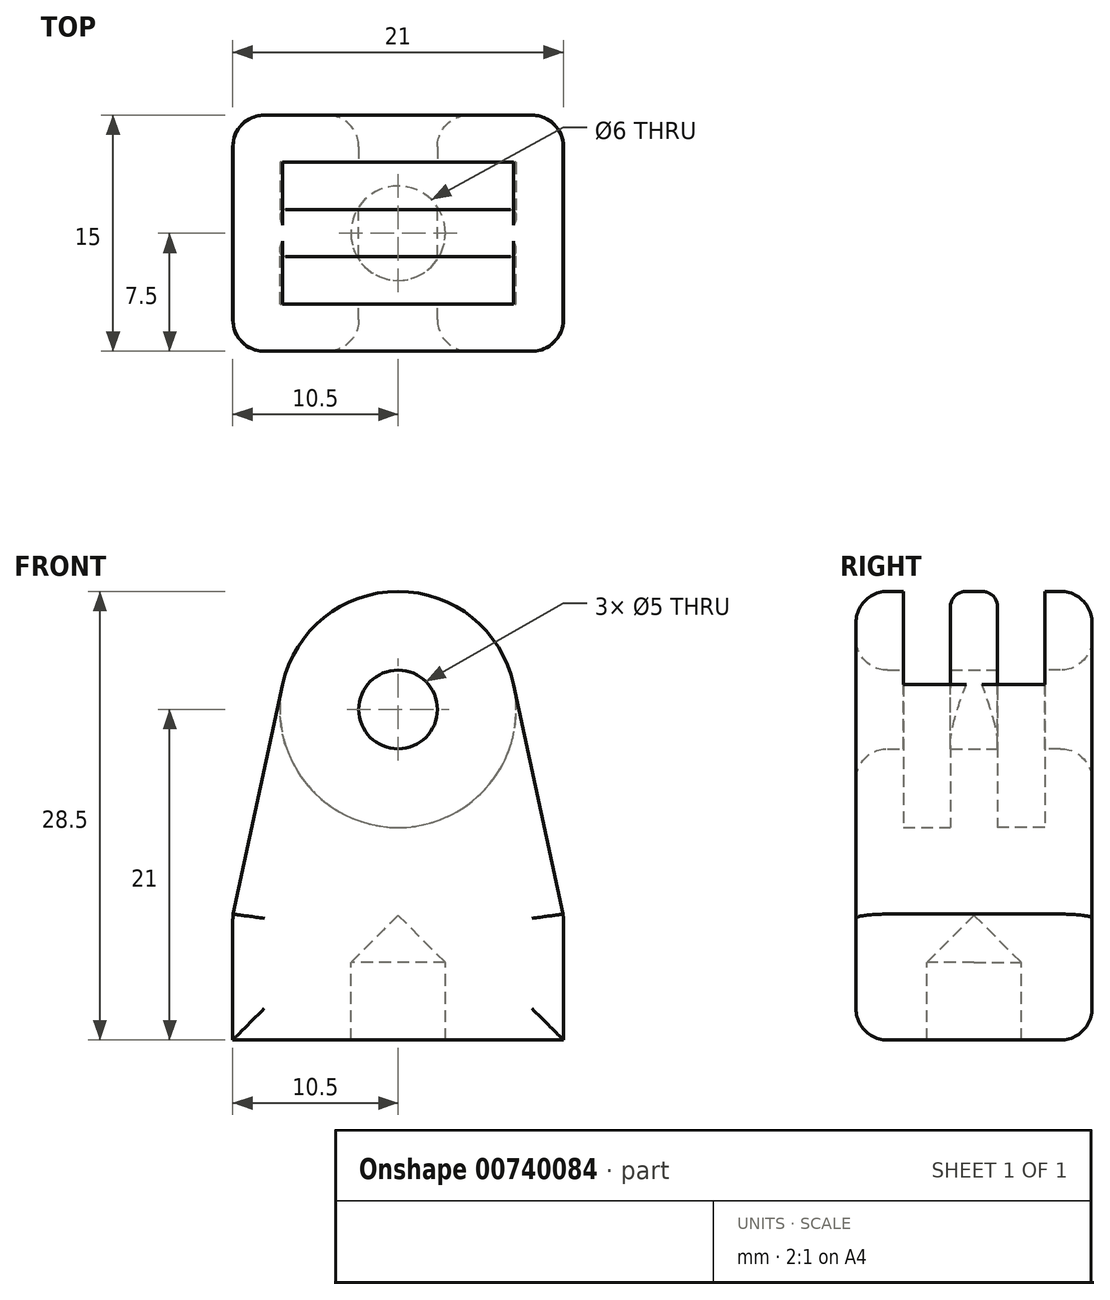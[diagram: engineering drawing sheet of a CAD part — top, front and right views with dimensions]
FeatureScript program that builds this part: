
annotation { "Feature Type Name" : "Feature", "Feature Type Description" : "" }
export const myFeature = defineFeature(function(context is Context, id is Id, definition is map)
    precondition{}
    {
        {
            var Q0;
            Q0=qCreatedBy(makeId("Front.planeOp"),FACE);
            var sketch = newSketch(context, id + "F0", { "sketchPlane" : qUnion([Q0])});
            skCircle(sketch, "E0", {"center": v(0, 0) * mm, "radius": 2.5 * mm});
            skCircle(sketch, "E1", {"center": v(0, 0) * mm, "radius": 7.5 * mm});
            skLineSegment(sketch, "E2", {"start": v(-7.33, 1.58) * mm, "end": v(-10.5, -13.08) * mm});
            skLineSegment(sketch, "E3", {"start": v(7.33, 1.58) * mm, "end": v(10.5, -13.08) * mm});
            skLineSegment(sketch, "E4", {"start": v(-10.5, -13.08) * mm, "end": v(10.5, -13.08) * mm});
            skSolve(sketch);
        }
        {
            var Q0;
            Q0=makeQuery(id+"F0.imprint","IMPRINT",FACE,{"disambiguationData":[TD([[makeQuery(id+"F0.imprint","IMPRINT",EDGE,{"derivedFrom":sQuery(id+"F0.wireOp",EDGE,"E0")}),-1.0]])]});
            extrude(context, id + "F1", {"entities" : qUnion([Q0]), "depth" : (7.5) * mm, "offsetDistance" : 25 * mm});
        }
        {
            var Q0;
            Q0=qCreatedBy(makeId("Front.planeOp"),FACE);
            cPlane(context, id + "F2", {"entities" : qUnion([Q0]), "cplaneType" : CPlaneType.OFFSET, "offset" : 1.5 * mm, "width" : 150 * mm, "height" : 150 * mm});
        }
        {
            var Q0;
            Q0=qCreatedBy(id+"F2.planeOp",FACE);
            var sketch = newSketch(context, id + "F3", { "sketchPlane" : qUnion([Q0])});
            skCircle(sketch, "E5", {"center": v(0, 0) * mm, "radius": 2.5 * mm});
            skCircle(sketch, "E6", {"center": v(0, 0) * mm, "radius": 7.5 * mm});
            skLineSegment(sketch, "E7", {"start": v(-7.33, 1.58) * mm, "end": v(-10.5, -13.08) * mm});
            skLineSegment(sketch, "E8", {"start": v(7.33, 1.58) * mm, "end": v(10.5, -13.08) * mm});
            skLineSegment(sketch, "E9", {"start": v(-10.5, -13.08) * mm, "end": v(10.5, -13.08) * mm});
            skSolve(sketch);
        }
        {
            var Q0;
            Q0=makeQuery(id+"F3.imprint","IMPRINT",FACE,{"disambiguationData":[TD([[makeQuery(id+"F3.imprint","IMPRINT",EDGE,{"derivedFrom":sQuery(id+"F3.wireOp",EDGE,"E5")}),-1.0]])]});
            extrude(context, id + "F4", {"entities" : qUnion([Q0]), "operationType" : NewBodyOperationType.REMOVE, "depth" : 3 * mm, "offsetDistance" : 25 * mm});
        }
        {
            var Q0;
            {var subQ0=sQuery(id+"F0.wireOp",EDGE,"E2");Q0=makeQuery(id+"F0.imprint","IMPRINT",FACE,{"disambiguationData":[TD([[makeQuery(id+"F0.imprint","IMPRINT",EDGE,{"derivedFrom":subQ0}),1.0]])]});}
            extrude(context, id + "F5", {"entities" : qUnion([Q0]), "operationType" : NewBodyOperationType.ADD, "depth" : 7.5 * mm, "offsetDistance" : 25 * mm});
        }
        {
            var Q0;
            Q0=makeQuery(id+"F4.boolean.opBoolean","SPLIT",BODY,{"disambiguationData":[OD(0.0)],"derivedFrom":makeQuery(id+"F1.opExtrude","SWEPT_BODY",BODY,{"disambiguationData":[OSD([sQuery(id+"F0.wireOp",EDGE,"E0"),sQuery(id+"F0.wireOp",EDGE,"E1")])]})});
            var Q1;
            Q1=qCreatedBy(makeId("Front.planeOp"),FACE);
            mirror(context, id + "F6", {"operationType" : NewBodyOperationType.ADD, "entities" : qUnion([Q0]), "mirrorPlane" : qUnion([Q1])});
        }
        {
            var Q0;
            Q0=qCreatedBy(makeId("Top.planeOp"),FACE);
            cPlane(context, id + "F7", {"entities" : qUnion([Q0]), "cplaneType" : CPlaneType.OFFSET, "offset" : 13 * mm, "oppositeDirection" : true, "width" : 150 * mm, "height" : 150 * mm});
        }
        {
            var Q0;
            Q0=qCreatedBy(id+"F7.planeOp",FACE);
            var sketch = newSketch(context, id + "F8", { "sketchPlane" : qUnion([Q0])});
            skCircle(sketch, "E10", {"center": v(0, 0) * mm, "radius": 3 * mm});
            skLineSegment(sketch, "E11.bottom", {"start": v(10.5, 7.5) * mm, "end": v(-10.5, 7.5) * mm});
            skLineSegment(sketch, "E11.top", {"start": v(10.5, -7.5) * mm, "end": v(-10.5, -7.5) * mm});
            skLineSegment(sketch, "E11.left", {"start": v(10.5, 7.5) * mm, "end": v(10.5, -7.5) * mm});
            skLineSegment(sketch, "E11.right", {"start": v(-10.5, 7.5) * mm, "end": v(-10.5, -7.5) * mm});
            skSolve(sketch);
        }
        {
            var Q0;
            Q0=makeQuery(id+"F8.imprint","IMPRINT",FACE,{"disambiguationData":[TD([[makeQuery(id+"F8.imprint","IMPRINT",EDGE,{"derivedFrom":sQuery(id+"F8.wireOp",EDGE,"E10")}),-1.0]])]});
            extrude(context, id + "F9", {"entities" : qUnion([Q0]), "operationType" : NewBodyOperationType.ADD, "oppositeDirection" : true, "depth" : 8 * mm, "offsetDistance" : 25 * mm});
        }
        {
            var Q0;
            {var subQ0=makeQuery(id+"F5.opExtrude","SWEPT_FACE",FACE,{"disambiguationData":[OSD([sQuery(id+"F0.wireOp",EDGE,"E4")])]});Q0=makeQuery(id+"F9.boolean.opBoolean","INTERSECT",EDGE,{"derivedFrom":[makeQuery(id+"F6.boolean.opBoolean","MERGE",FACE,{"derivedFrom":[subQ0,makeQuery(id+"F6.opPattern","COPY",FACE,{"derivedFrom":subQ0,"instanceName":"1"})]}),makeQuery(id+"F9.opExtrude","SWEPT_FACE",FACE,{"disambiguationData":[OSD([sQuery(id+"F8.wireOp",EDGE,"E10")])]})]});}
            chamfer(context, id + "F10", {"entities" : qUnion([Q0]), "width" : 3 * mm, "tangentPropagation" : true});
        }
        {
            var Q0;
            Q0=makeQuery(id+"F9.opExtrude","CAP_EDGE",EDGE,{"disambiguationData":[OSD([sQuery(id+"F8.wireOp",EDGE,"E11.left")])],"isStart":true});
            var Q1;
            Q1=makeQuery(id+"F9.opExtrude","CAP_EDGE",EDGE,{"disambiguationData":[OSD([sQuery(id+"F8.wireOp",EDGE,"E11.right")])],"isStart":true});
            fillet(context, id + "F11", {"entities" : qUnion([Q0, Q1]), "radius" : 10 * mm, "tangentPropagation" : true, "allowEdgeOverflow" : false});
        }
        {
            var Q0;
            Q0=makeQuery(id+"F5.opExtrude","CAP_EDGE",EDGE,{"disambiguationData":[OSD([sQuery(id+"F0.wireOp",EDGE,"E2")])],"isStart":false});
            var Q1;
            Q1=makeQuery(id+"F9.opExtrude","SWEPT_EDGE",EDGE,{"disambiguationData":[OSD([sQuery(id+"F8.wireOp",EDGE,"E11.top"),sQuery(id+"F8.wireOp",EDGE,"E11.right")])]});
            var Q2;
            Q2=makeQuery(id+"F9.opExtrude","SWEPT_EDGE",EDGE,{"disambiguationData":[OSD([sQuery(id+"F8.wireOp",EDGE,"E11.top"),sQuery(id+"F8.wireOp",EDGE,"E11.left")])]});
            var Q3;
            {var subQ0=sQuery(id+"F0.wireOp",EDGE,"E1");Q3=makeQuery(id+"F11.opFillet","BLEND_EDGE",EDGE,{"blendedFrom":[makeQuery(id+"F9.opExtrude","CAP_EDGE",EDGE,{"disambiguationData":[OSD([sQuery(id+"F8.wireOp",EDGE,"E11.left")])],"isStart":true}),makeQuery(id+"F9.boolean.opBoolean","MERGE",FACE,{"derivedFrom":[makeQuery(id+"F5.boolean.opBoolean","MERGE",FACE,{"derivedFrom":[makeQuery(id+"F1.opExtrude","CAP_FACE",FACE,{"disambiguationData":[OSD([sQuery(id+"F0.wireOp",EDGE,"E0"),subQ0])],"isStart":false}),makeQuery(id+"F5.opExtrude","CAP_FACE",FACE,{"disambiguationData":[OSD([subQ0,sQuery(id+"F0.wireOp",EDGE,"E2"),sQuery(id+"F0.wireOp",EDGE,"E3"),sQuery(id+"F0.wireOp",EDGE,"E4")])],"isStart":false})]}),makeQuery(id+"F9.opExtrude","SWEPT_FACE",FACE,{"disambiguationData":[OSD([sQuery(id+"F8.wireOp",EDGE,"E11.top")])]})]})],"blendedInto":[makeQuery(id+"F9.boolean.opBoolean","MERGE",FACE,{"derivedFrom":[makeQuery(id+"F5.boolean.opBoolean","MERGE",FACE,{"derivedFrom":[makeQuery(id+"F1.opExtrude","CAP_FACE",FACE,{"disambiguationData":[OSD([sQuery(id+"F0.wireOp",EDGE,"E0"),subQ0])],"isStart":false}),makeQuery(id+"F5.opExtrude","CAP_FACE",FACE,{"disambiguationData":[OSD([subQ0,sQuery(id+"F0.wireOp",EDGE,"E2"),sQuery(id+"F0.wireOp",EDGE,"E3"),sQuery(id+"F0.wireOp",EDGE,"E4")])],"isStart":false})]}),makeQuery(id+"F9.opExtrude","SWEPT_FACE",FACE,{"disambiguationData":[OSD([sQuery(id+"F8.wireOp",EDGE,"E11.top")])]})]})]});}
            var Q4;
            {var subQ0=sQuery(id+"F0.wireOp",EDGE,"E1");Q4=makeQuery(id+"F11.opFillet","BLEND_EDGE",EDGE,{"blendedFrom":[makeQuery(id+"F9.opExtrude","CAP_EDGE",EDGE,{"disambiguationData":[OSD([sQuery(id+"F8.wireOp",EDGE,"E11.right")])],"isStart":true}),makeQuery(id+"F9.boolean.opBoolean","MERGE",FACE,{"derivedFrom":[makeQuery(id+"F5.boolean.opBoolean","MERGE",FACE,{"derivedFrom":[makeQuery(id+"F1.opExtrude","CAP_FACE",FACE,{"disambiguationData":[OSD([sQuery(id+"F0.wireOp",EDGE,"E0"),subQ0])],"isStart":false}),makeQuery(id+"F5.opExtrude","CAP_FACE",FACE,{"disambiguationData":[OSD([subQ0,sQuery(id+"F0.wireOp",EDGE,"E2"),sQuery(id+"F0.wireOp",EDGE,"E3"),sQuery(id+"F0.wireOp",EDGE,"E4")])],"isStart":false})]}),makeQuery(id+"F9.opExtrude","SWEPT_FACE",FACE,{"disambiguationData":[OSD([sQuery(id+"F8.wireOp",EDGE,"E11.top")])]})]})],"blendedInto":[makeQuery(id+"F9.boolean.opBoolean","MERGE",FACE,{"derivedFrom":[makeQuery(id+"F5.boolean.opBoolean","MERGE",FACE,{"derivedFrom":[makeQuery(id+"F1.opExtrude","CAP_FACE",FACE,{"disambiguationData":[OSD([sQuery(id+"F0.wireOp",EDGE,"E0"),subQ0])],"isStart":false}),makeQuery(id+"F5.opExtrude","CAP_FACE",FACE,{"disambiguationData":[OSD([subQ0,sQuery(id+"F0.wireOp",EDGE,"E2"),sQuery(id+"F0.wireOp",EDGE,"E3"),sQuery(id+"F0.wireOp",EDGE,"E4")])],"isStart":false})]}),makeQuery(id+"F9.opExtrude","SWEPT_FACE",FACE,{"disambiguationData":[OSD([sQuery(id+"F8.wireOp",EDGE,"E11.top")])]})]})]});}
            var Q5;
            Q5=makeQuery(id+"F6.opPattern","COPY",EDGE,{"derivedFrom":makeQuery(id+"F5.opExtrude","CAP_EDGE",EDGE,{"disambiguationData":[OSD([sQuery(id+"F0.wireOp",EDGE,"E3")])],"isStart":false}),"instanceName":"1"});
            var Q6;
            Q6=makeQuery(id+"F9.opExtrude","SWEPT_EDGE",EDGE,{"disambiguationData":[OSD([sQuery(id+"F8.wireOp",EDGE,"E11.bottom"),sQuery(id+"F8.wireOp",EDGE,"E11.left")])]});
            var Q7;
            {var subQ0=sQuery(id+"F0.wireOp",EDGE,"E1");Q7=makeQuery(id+"F11.opFillet","BLEND_EDGE",EDGE,{"blendedFrom":[makeQuery(id+"F9.opExtrude","CAP_EDGE",EDGE,{"disambiguationData":[OSD([sQuery(id+"F8.wireOp",EDGE,"E11.left")])],"isStart":true}),makeQuery(id+"F9.boolean.opBoolean","MERGE",FACE,{"derivedFrom":[makeQuery(id+"F6.opPattern","COPY",FACE,{"derivedFrom":makeQuery(id+"F5.boolean.opBoolean","MERGE",FACE,{"derivedFrom":[makeQuery(id+"F1.opExtrude","CAP_FACE",FACE,{"disambiguationData":[OSD([sQuery(id+"F0.wireOp",EDGE,"E0"),subQ0])],"isStart":false}),makeQuery(id+"F5.opExtrude","CAP_FACE",FACE,{"disambiguationData":[OSD([subQ0,sQuery(id+"F0.wireOp",EDGE,"E2"),sQuery(id+"F0.wireOp",EDGE,"E3"),sQuery(id+"F0.wireOp",EDGE,"E4")])],"isStart":false})]}),"instanceName":"1"}),makeQuery(id+"F9.opExtrude","SWEPT_FACE",FACE,{"disambiguationData":[OSD([sQuery(id+"F8.wireOp",EDGE,"E11.bottom")])]})]})],"blendedInto":[makeQuery(id+"F9.boolean.opBoolean","MERGE",FACE,{"derivedFrom":[makeQuery(id+"F6.opPattern","COPY",FACE,{"derivedFrom":makeQuery(id+"F5.boolean.opBoolean","MERGE",FACE,{"derivedFrom":[makeQuery(id+"F1.opExtrude","CAP_FACE",FACE,{"disambiguationData":[OSD([sQuery(id+"F0.wireOp",EDGE,"E0"),subQ0])],"isStart":false}),makeQuery(id+"F5.opExtrude","CAP_FACE",FACE,{"disambiguationData":[OSD([subQ0,sQuery(id+"F0.wireOp",EDGE,"E2"),sQuery(id+"F0.wireOp",EDGE,"E3"),sQuery(id+"F0.wireOp",EDGE,"E4")])],"isStart":false})]}),"instanceName":"1"}),makeQuery(id+"F9.opExtrude","SWEPT_FACE",FACE,{"disambiguationData":[OSD([sQuery(id+"F8.wireOp",EDGE,"E11.bottom")])]})]})]});}
            var Q8;
            Q8=makeQuery(id+"F9.opExtrude","SWEPT_EDGE",EDGE,{"disambiguationData":[OSD([sQuery(id+"F8.wireOp",EDGE,"E11.bottom"),sQuery(id+"F8.wireOp",EDGE,"E11.right")])]});
            var Q9;
            {var subQ0=sQuery(id+"F0.wireOp",EDGE,"E1");Q9=makeQuery(id+"F11.opFillet","BLEND_EDGE",EDGE,{"blendedFrom":[makeQuery(id+"F9.opExtrude","CAP_EDGE",EDGE,{"disambiguationData":[OSD([sQuery(id+"F8.wireOp",EDGE,"E11.right")])],"isStart":true}),makeQuery(id+"F9.boolean.opBoolean","MERGE",FACE,{"derivedFrom":[makeQuery(id+"F6.opPattern","COPY",FACE,{"derivedFrom":makeQuery(id+"F5.boolean.opBoolean","MERGE",FACE,{"derivedFrom":[makeQuery(id+"F1.opExtrude","CAP_FACE",FACE,{"disambiguationData":[OSD([sQuery(id+"F0.wireOp",EDGE,"E0"),subQ0])],"isStart":false}),makeQuery(id+"F5.opExtrude","CAP_FACE",FACE,{"disambiguationData":[OSD([subQ0,sQuery(id+"F0.wireOp",EDGE,"E2"),sQuery(id+"F0.wireOp",EDGE,"E3"),sQuery(id+"F0.wireOp",EDGE,"E4")])],"isStart":false})]}),"instanceName":"1"}),makeQuery(id+"F9.opExtrude","SWEPT_FACE",FACE,{"disambiguationData":[OSD([sQuery(id+"F8.wireOp",EDGE,"E11.bottom")])]})]})],"blendedInto":[makeQuery(id+"F9.boolean.opBoolean","MERGE",FACE,{"derivedFrom":[makeQuery(id+"F6.opPattern","COPY",FACE,{"derivedFrom":makeQuery(id+"F5.boolean.opBoolean","MERGE",FACE,{"derivedFrom":[makeQuery(id+"F1.opExtrude","CAP_FACE",FACE,{"disambiguationData":[OSD([sQuery(id+"F0.wireOp",EDGE,"E0"),subQ0])],"isStart":false}),makeQuery(id+"F5.opExtrude","CAP_FACE",FACE,{"disambiguationData":[OSD([subQ0,sQuery(id+"F0.wireOp",EDGE,"E2"),sQuery(id+"F0.wireOp",EDGE,"E3"),sQuery(id+"F0.wireOp",EDGE,"E4")])],"isStart":false})]}),"instanceName":"1"}),makeQuery(id+"F9.opExtrude","SWEPT_FACE",FACE,{"disambiguationData":[OSD([sQuery(id+"F8.wireOp",EDGE,"E11.bottom")])]})]})]});}
            var Q10;
            {var subQ0=sQuery(id+"F0.wireOp",EDGE,"E1");Q10=makeQuery(id+"F9.boolean.opBoolean","MERGE",FACE,{"derivedFrom":[makeQuery(id+"F6.opPattern","COPY",FACE,{"derivedFrom":makeQuery(id+"F5.boolean.opBoolean","MERGE",FACE,{"derivedFrom":[makeQuery(id+"F1.opExtrude","CAP_FACE",FACE,{"disambiguationData":[OSD([sQuery(id+"F0.wireOp",EDGE,"E0"),subQ0])],"isStart":false}),makeQuery(id+"F5.opExtrude","CAP_FACE",FACE,{"disambiguationData":[OSD([subQ0,sQuery(id+"F0.wireOp",EDGE,"E2"),sQuery(id+"F0.wireOp",EDGE,"E3"),sQuery(id+"F0.wireOp",EDGE,"E4")])],"isStart":false})]}),"instanceName":"1"}),makeQuery(id+"F9.opExtrude","SWEPT_FACE",FACE,{"disambiguationData":[OSD([sQuery(id+"F8.wireOp",EDGE,"E11.bottom")])]})]});}
            var Q11;
            {var subQ0=sQuery(id+"F0.wireOp",EDGE,"E1");Q11=makeQuery(id+"F9.boolean.opBoolean","MERGE",FACE,{"derivedFrom":[makeQuery(id+"F5.boolean.opBoolean","MERGE",FACE,{"derivedFrom":[makeQuery(id+"F1.opExtrude","CAP_FACE",FACE,{"disambiguationData":[OSD([sQuery(id+"F0.wireOp",EDGE,"E0"),subQ0])],"isStart":false}),makeQuery(id+"F5.opExtrude","CAP_FACE",FACE,{"disambiguationData":[OSD([subQ0,sQuery(id+"F0.wireOp",EDGE,"E2"),sQuery(id+"F0.wireOp",EDGE,"E3"),sQuery(id+"F0.wireOp",EDGE,"E4")])],"isStart":false})]}),makeQuery(id+"F9.opExtrude","SWEPT_FACE",FACE,{"disambiguationData":[OSD([sQuery(id+"F8.wireOp",EDGE,"E11.top")])]})]});}
            fillet(context, id + "F12", {"entities" : qUnion([Q0, Q1, Q2, Q3, Q4, Q5, Q6, Q7, Q8, Q9, Q10, Q11]), "radius" : 2 * mm, "tangentPropagation" : true, "allowEdgeOverflow" : false});
        }
        {
            var Q0;
            {var subQ0=sQuery(id+"F3.wireOp",EDGE,"E6");Q0=makeQuery(id+"F5.boolean.opBoolean","SPLIT",EDGE,{"disambiguationData":[topologyDisambiguationEdgeConnected([makeQuery(id+"F1.opExtrude","SWEPT_FACE",FACE,{"disambiguationData":[OSD([sQuery(id+"F0.wireOp",EDGE,"E1")])]})])],"derivedFrom":makeQuery(id+"F4.boolean.opBoolean","COPY",EDGE,{"derivedFrom":makeQuery(id+"F4.opExtrude","CAP_EDGE",EDGE,{"disambiguationData":[OSD([subQ0])],"isStart":false})})});}
            var Q1;
            {var subQ0=sQuery(id+"F3.wireOp",EDGE,"E6");Q1=makeQuery(id+"F6.opPattern","COPY",EDGE,{"derivedFrom":makeQuery(id+"F5.boolean.opBoolean","SPLIT",EDGE,{"disambiguationData":[topologyDisambiguationEdgeConnected([makeQuery(id+"F1.opExtrude","SWEPT_FACE",FACE,{"disambiguationData":[OSD([sQuery(id+"F0.wireOp",EDGE,"E1")])]})])],"derivedFrom":makeQuery(id+"F4.boolean.opBoolean","COPY",EDGE,{"derivedFrom":makeQuery(id+"F4.opExtrude","CAP_EDGE",EDGE,{"disambiguationData":[OSD([subQ0])],"isStart":true})})}),"instanceName":"1"});}
            var Q2;
            {var subQ0=sQuery(id+"F3.wireOp",EDGE,"E6");Q2=makeQuery(id+"F5.boolean.opBoolean","SPLIT",EDGE,{"disambiguationData":[topologyDisambiguationEdgeConnected([makeQuery(id+"F1.opExtrude","SWEPT_FACE",FACE,{"disambiguationData":[OSD([sQuery(id+"F0.wireOp",EDGE,"E1")])]})])],"derivedFrom":makeQuery(id+"F4.boolean.opBoolean","COPY",EDGE,{"derivedFrom":makeQuery(id+"F4.opExtrude","CAP_EDGE",EDGE,{"disambiguationData":[OSD([subQ0])],"isStart":true})})});}
            var Q3;
            {var subQ0=sQuery(id+"F3.wireOp",EDGE,"E6");Q3=makeQuery(id+"F6.opPattern","COPY",EDGE,{"derivedFrom":makeQuery(id+"F5.boolean.opBoolean","SPLIT",EDGE,{"disambiguationData":[topologyDisambiguationEdgeConnected([makeQuery(id+"F1.opExtrude","SWEPT_FACE",FACE,{"disambiguationData":[OSD([sQuery(id+"F0.wireOp",EDGE,"E1")])]})])],"derivedFrom":makeQuery(id+"F4.boolean.opBoolean","COPY",EDGE,{"derivedFrom":makeQuery(id+"F4.opExtrude","CAP_EDGE",EDGE,{"disambiguationData":[OSD([subQ0])],"isStart":false})})}),"instanceName":"1"});}
            fillet(context, id + "F13", {"entities" : qUnion([Q0, Q1, Q2, Q3]), "radius" : 1 * mm, "tangentPropagation" : true, "allowEdgeOverflow" : false});
        }
    });
